# Revit family: Cleanout_Floor-Zurn-Z1400-K
name_source: partatom
category: Plumbing Fixtures
units: mm (PartAtom-declared; Revit-internal decimal feet)

## family parameters
Always vertical = Yes
Cut with Voids When Loaded = No
Maintain Annotation Orientation = No
OmniClass Number = 23.70.50.21.24.14
OmniClass Title = Deck Waste Water Drains
Part Type = Normal
Room Calculation Point = No
Round Connector Dimension = Use Radius
Shared = No
Work Plane-Based = No

## types (68) — shared parameters
Assembly Code = D2030300
CW Connection = No
Default Elevation = 20 "
Description = HEAVY-DUTY LEVEL-TROL ADJUSTABLE FLOOR CLEANOUT W/ ANCHOR FLANGE
HW Connection = No
Main Material = Iron - Zurn - Cast - Painted - Blue
Manufacturer = Zurn Water, LLC
Manufacurer Brand = Zurn
Modified Date = 02/06/2026
Product Documentation Link = https://files.zurn.com
Product Page URL = https://www.zurn.com
Product data url = https://www.bimobject.com
URL = www.zurn.com
Vent Connection = No
WFU = 1
Waste Connection = Yes
ZS = No
zero-valued in all types: CWFU, Grate Open Area, HWFU

## per-type parameters (varying)
| type | Approx. Weight (Lbs) | Connector Radius | Dimension "B" | Dimension "C" | Dimension "E" | Grate Diameter | Model | Pipe Size_A Inside Diameter | Pipe Size_A Nominal Diameter | Pipe Size_A Outer Diameter | Top Material | Type Comments | Z | ZB/ZN |
| Z1400-K 2IC | 18.1 " | 1 " | 9.5 " | 6.125 " | 6.875 " | 2.782 " | Z1400-K | 2.067 " | 2 " | 2.375 " | Iron - Zurn - Cast - Painted - Blue | Z1400-K 2 Inch Inside Caulk | Yes | No |
| Z1400-K-3IC | 18.8 " | 1.5 " | 9.5 " | 6.125 " | 6.875 " | 2.782 " | Z1400-K | 3.068 " | 3 " | 3.5 " | Iron - Zurn - Cast - Painted - Blue | Z1400-K 3 Inch Inside Caulk | Yes | No |
| Z1400-K-4IC | 20.3 " | 2 " | 11.5 " | 7.25 " | 6.875 " | 3.344 " | Z1400-K | 4.026 " | 4 " | 4.5 " | Iron - Zurn - Cast - Painted - Blue | Z1400-K 4 Inch Inside Caulk | Yes | No |
| Z1400-K-5IC | 25.2 " | 2.5 " | 11.5 " | 8.25 " | 6.875 " | 3.844 " | Z1400-K | 5.047 " | 5 " | 5.563 " | Iron - Zurn - Cast - Painted - Blue | Z1400-K 5 Inch Inside Caulk | Yes | No |
| Z1400-K-6IC | 39.2 " | 3 " | 12.25 " | 9.25 " | 6.875 " | 4.344 " | Z1400-K | 6.065 " | 6 " | 6.625 " | Iron - Zurn - Cast - Painted - Blue | Z1400-K 6 Inch Inside Caulk | Yes | No |
| Z1400-K 2NH | 11.3 " | 1 " | 7.5 " | 4.125 " | 4.625 " | 1.782 " | Z1400-K | 2.067 " | 2 " | 2.375 " | Iron - Zurn - Cast - Painted - Blue | Z1400-K 2 Inch No-Hub | Yes | No |
| Z1400-K-3NH | 10 " | 1.5 " | 7.5 " | 5.125 " | 5.375 " | 2.282 " | Z1400-K | 3.068 " | 3 " | 3.5 " | Iron - Zurn - Cast - Painted - Blue | Z1400-K 3 Inch No-Hub | Yes | No |
| Z1400-K-4NH | 12.6 " | 2 " | 7.5 " | 5.125 " | 5.375 " | 2.282 " | Z1400-K | 4.026 " | 4 " | 4.5 " | Iron - Zurn - Cast - Painted - Blue | Z1400-K 4 Inch No-Hub | Yes | No |
| Z1400-K-5NH | 20.2 " | 2.5 " | 11.5 " | 7.25 " | 7.5 " | 3.344 " | Z1400-K | 5.047 " | 5 " | 5.563 " | Iron - Zurn - Cast - Painted - Blue | Z1400-K 5 Inch No-Hub | Yes | No |
| Z1400-K-6NH | 29.2 " | 3 " | 11.5 " | 8.125 " | 4.75 " | 3.782 " | Z1400-K | 6.065 " | 6 " | 6.625 " | Iron - Zurn - Cast - Painted - Blue | Z1400-K 6 Inch No-Hub | Yes | No |
| Z1400-K-8NH | 37.9 " | 4 " | 12.25 " | 9.25 " | 7.5 " | 4.344 " | Z1400-K | 7.981 " | 8 " | 8.625 " | Iron - Zurn - Cast - Painted - Blue | Z1400-K 8 Inch No-Hub | Yes | No |
| Z1400-K 2NL | 12.2 " | 1 " | 7.5 " | 5.125 " | 5.375 " | 2.282 " | Z1400-K | 2.067 " | 2 " | 2.375 " | Iron - Zurn - Cast - Painted - Blue | Z1400-K 2 Inch Neo-Loc | Yes | No |
| Z1400-K-3NL | 12.9 " | 1.5 " | 7.5 " | 5.125 " | 5.375 " | 2.282 " | Z1400-K | 3.068 " | 3 " | 3.5 " | Iron - Zurn - Cast - Painted - Blue | Z1400-K 3 Inch Neo-Loc | Yes | No |
| Z1400-K-4NL | 14.2 " | 2 " | 7.5 " | 5.125 " | 5.375 " | 2.282 " | Z1400-K | 4.026 " | 4 " | 4.5 " | Iron - Zurn - Cast - Painted - Blue | Z1400-K 4 Inch Neo-Loc | Yes | No |
| Z1400-K-5NL | 21.3 " | 2.5 " | 11.5 " | 7.25 " | 6.5 " | 3.344 " | Z1400-K | 5.047 " | 5 " | 5.563 " | Iron - Zurn - Cast - Painted - Blue | Z1400-K 5 Inch Neo-Loc | Yes | No |
| Z1400-K-6NL | 28.9 " | 3 " | 11.5 " | 8.25 " | 5.875 " | 3.844 " | Z1400-K | 6.065 " | 6 " | 6.625 " | Iron - Zurn - Cast - Painted - Blue | Z1400-K 6 Inch Neo-Loc | Yes | No |
| Z1400-K-8NL | 31.5 " | 4 " | 12.25 " | 9.25 " | 6.5 " | 4.344 " | Z1400-K | 7.981 " | 8 " | 8.625 " | Iron - Zurn - Cast - Painted - Blue | Z1400-K 8 Inch Neo-Loc | Yes | No |
| ZB1400-K 2IC | 18.1 " | 1 " | 9.5 " | 6.125 " | 6.875 " | 2.782 " | ZB1400-K | 2.067 " | 2 " | 2.375 " | Bronze - Zurn - Polished | ZB1400-K 2 Inch Inside Caulk | No | Yes |
| ZB1400-K-3IC | 18.8 " | 1.5 " | 9.5 " | 6.125 " | 6.875 " | 2.782 " | ZB1400-K | 3.068 " | 3 " | 3.5 " | Bronze - Zurn - Polished | ZB1400-K 3 Inch Inside Caulk | No | Yes |
| ZB1400-K-4IC | 20.3 " | 2 " | 11.5 " | 7.25 " | 6.875 " | 3.344 " | ZB1400-K | 4.026 " | 4 " | 4.5 " | Bronze - Zurn - Polished | ZB1400-K 4 Inch Inside Caulk | No | Yes |
| ZB1400-K-5IC | 25.2 " | 2.5 " | 11.5 " | 8.25 " | 6.875 " | 3.844 " | ZB1400-K | 5.047 " | 5 " | 5.563 " | Bronze - Zurn - Polished | ZB1400-K 5 Inch Inside Caulk | No | Yes |
| ZB1400-K-6IC | 39.2 " | 3 " | 12.25 " | 9.25 " | 6.875 " | 4.344 " | ZB1400-K | 6.065 " | 6 " | 6.625 " | Bronze - Zurn - Polished | ZB1400-K 6 Inch Inside Caulk | No | Yes |
| ZB1400-K 2NH | 11.3 " | 1 " | 7.5 " | 4.125 " | 4.625 " | 1.782 " | ZB1400-K | 2.067 " | 2 " | 2.375 " | Bronze - Zurn - Polished | ZB1400-K 2 Inch No-Hub | No | Yes |
| ZB1400-K-3NH | 10 " | 1.5 " | 7.5 " | 5.125 " | 5.375 " | 2.282 " | ZB1400-K | 3.068 " | 3 " | 3.5 " | Bronze - Zurn - Polished | ZB1400-K 3 Inch No-Hub | No | Yes |
| ZB1400-K-4NH | 12.6 " | 2 " | 7.5 " | 5.125 " | 5.375 " | 2.282 " | ZB1400-K | 4.026 " | 4 " | 4.5 " | Bronze - Zurn - Polished | ZB1400-K 4 Inch No-Hub | No | Yes |
| ZB1400-K-5NH | 20.2 " | 2.5 " | 11.5 " | 7.25 " | 7.5 " | 3.344 " | ZB1400-K | 5.047 " | 5 " | 5.563 " | Bronze - Zurn - Polished | ZB1400-K 5 Inch No-Hub | No | Yes |
| ZB1400-K-6NH | 29.2 " | 3 " | 11.5 " | 8.125 " | 4.75 " | 3.782 " | ZB1400-K | 6.065 " | 6 " | 6.625 " | Bronze - Zurn - Polished | ZB1400-K 6 Inch No-Hub | No | Yes |
| ZB1400-K-8NH | 37.9 " | 4 " | 12.25 " | 9.25 " | 7.5 " | 4.344 " | ZB1400-K | 7.981 " | 8 " | 8.625 " | Bronze - Zurn - Polished | ZB1400-K 8 Inch No-Hub | No | Yes |
| ZB1400-K 2NL | 12.2 " | 1 " | 7.5 " | 5.125 " | 5.375 " | 2.282 " | ZB1400-K | 2.067 " | 2 " | 2.375 " | Bronze - Zurn - Polished | ZB1400-K 2 Inch Neo-Loc | No | Yes |
| ZB1400-K-3NL | 12.9 " | 1.5 " | 7.5 " | 5.125 " | 5.375 " | 2.282 " | ZB1400-K | 3.068 " | 3 " | 3.5 " | Bronze - Zurn - Polished | ZB1400-K 3 Inch Neo-Loc | No | Yes |
| ZB1400-K-4NL | 14.2 " | 2 " | 7.5 " | 5.125 " | 5.375 " | 2.282 " | ZB1400-K | 4.026 " | 4 " | 4.5 " | Bronze - Zurn - Polished | ZB1400-K 4 Inch Neo-Loc | No | Yes |
| ZB1400-K-5NL | 21.3 " | 2.5 " | 11.5 " | 7.25 " | 6.5 " | 3.344 " | ZB1400-K | 5.047 " | 5 " | 5.563 " | Bronze - Zurn - Polished | ZB1400-K 5 Inch Neo-Loc | No | Yes |
| ZB1400-K-6NL | 28.9 " | 3 " | 11.5 " | 8.25 " | 5.875 " | 3.844 " | ZB1400-K | 6.065 " | 6 " | 6.625 " | Bronze - Zurn - Polished | ZB1400-K 6 Inch Neo-Loc | No | Yes |
| ZB1400-K-8NL | 31.5 " | 4 " | 12.25 " | 9.25 " | 6.5 " | 4.344 " | ZB1400-K | 7.981 " | 8 " | 8.625 " | Bronze - Zurn - Polished | ZB1400-K 8 Inch Neo-Loc | No | Yes |
| ZN1400-K 2IC | 18.1 " | 1 " | 9.5 " | 6.125 " | 6.875 " | 2.782 " | ZN1400-K | 2.067 " | 2 " | 2.375 " | Bronze - Zurn - Polished Nickel | ZN1400-K 2 Inch Inside Caulk | No | Yes |
| ZN1400-K-3IC | 18.8 " | 1.5 " | 9.5 " | 6.125 " | 6.875 " | 2.782 " | ZN1400-K | 3.068 " | 3 " | 3.5 " | Bronze - Zurn - Polished Nickel | ZN1400-K 3 Inch Inside Caulk | No | Yes |
| ZN1400-K-4IC | 20.3 " | 2 " | 11.5 " | 7.25 " | 6.875 " | 3.344 " | ZN1400-K | 4.026 " | 4 " | 4.5 " | Bronze - Zurn - Polished Nickel | ZN1400-K 4 Inch Inside Caulk | No | Yes |
| ZN1400-K-5IC | 25.2 " | 2.5 " | 11.5 " | 8.25 " | 6.875 " | 3.844 " | ZN1400-K | 5.047 " | 5 " | 5.563 " | Bronze - Zurn - Polished Nickel | ZN1400-K 5 Inch Inside Caulk | No | Yes |
| ZN1400-K-6IC | 39.2 " | 3 " | 12.25 " | 9.25 " | 6.875 " | 4.344 " | ZN1400-K | 6.065 " | 6 " | 6.625 " | Bronze - Zurn - Polished Nickel | ZN1400-K 6 Inch Inside Caulk | No | Yes |
| ZN1400-K 2NH | 11.3 " | 1 " | 7.5 " | 4.125 " | 4.625 " | 1.782 " | ZN1400-K | 2.067 " | 2 " | 2.375 " | Bronze - Zurn - Polished Nickel | ZN1400-K 2 Inch No-Hub | No | Yes |
| ZN1400-K-3NH | 10 " | 1.5 " | 7.5 " | 5.125 " | 5.375 " | 2.282 " | ZN1400-K | 3.068 " | 3 " | 3.5 " | Bronze - Zurn - Polished Nickel | ZN1400-K 3 Inch No-Hub | No | Yes |
| ZN1400-K-4NH | 12.6 " | 2 " | 7.5 " | 5.125 " | 5.375 " | 2.282 " | ZN1400-K | 4.026 " | 4 " | 4.5 " | Bronze - Zurn - Polished Nickel | ZN1400-K 4 Inch No-Hub | No | Yes |
| ZN1400-K-5NH | 20.2 " | 2.5 " | 11.5 " | 7.25 " | 7.5 " | 3.344 " | ZN1400-K | 5.047 " | 5 " | 5.563 " | Bronze - Zurn - Polished Nickel | ZN1400-K 5 Inch No-Hub | No | Yes |
| ZN1400-K-6NH | 29.2 " | 3 " | 11.5 " | 8.125 " | 4.75 " | 3.782 " | ZN1400-K | 6.065 " | 6 " | 6.625 " | Bronze - Zurn - Polished Nickel | ZN1400-K 6 Inch No-Hub | No | Yes |
| ZN1400-K-8NH | 37.9 " | 4 " | 12.25 " | 9.25 " | 7.5 " | 4.344 " | ZN1400-K | 7.981 " | 8 " | 8.625 " | Bronze - Zurn - Polished Nickel | ZN1400-K 8 Inch No-Hub | No | Yes |
| ZN1400-K 2NL | 12.2 " | 1 " | 7.5 " | 5.125 " | 5.375 " | 2.282 " | ZN1400-K | 2.067 " | 2 " | 2.375 " | Bronze - Zurn - Polished Nickel | ZN1400-K 2 Inch Neo-Loc | No | Yes |
| ZN1400-K-3NL | 12.9 " | 1.5 " | 7.5 " | 5.125 " | 5.375 " | 2.282 " | ZN1400-K | 3.068 " | 3 " | 3.5 " | Bronze - Zurn - Polished Nickel | ZN1400-K 3 Inch Neo-Loc | No | Yes |
| ZN1400-K-4NL | 14.2 " | 2 " | 7.5 " | 5.125 " | 5.375 " | 2.282 " | ZN1400-K | 4.026 " | 4 " | 4.5 " | Bronze - Zurn - Polished Nickel | ZN1400-K 4 Inch Neo-Loc | No | Yes |
| ZN1400-K-5NL | 21.3 " | 2.5 " | 11.5 " | 7.25 " | 6.5 " | 3.344 " | ZN1400-K | 5.047 " | 5 " | 5.563 " | Bronze - Zurn - Polished Nickel | ZN1400-K 5 Inch Neo-Loc | No | Yes |
| ZN1400-K-6NL | 28.9 " | 3 " | 11.5 " | 8.25 " | 5.875 " | 3.844 " | ZN1400-K | 6.065 " | 6 " | 6.625 " | Bronze - Zurn - Polished Nickel | ZN1400-K 6 Inch Neo-Loc | No | Yes |
| ZN1400-K-8NL | 31.5 " | 4 " | 12.25 " | 9.25 " | 6.5 " | 4.344 " | ZN1400-K | 7.981 " | 8 " | 8.625 " | Bronze - Zurn - Polished Nickel | ZN1400-K 8 Inch Neo-Loc | No | Yes |
| ZS1400-K 2IC | 18.1 " | 1 " | 9.5 " | 6.125 " | 6.875 " | 2.782 " | ZS1400-K | 2.067 " | 2 " | 2.375 " | Steel - Zurn - Stainless - Type - 304 | ZS1400-K 2 Inch Inside Caulk | No | Yes |
| ZS1400-K-3IC | 18.8 " | 1.5 " | 9.5 " | 6.125 " | 6.875 " | 2.782 " | ZS1400-K | 3.068 " | 3 " | 3.5 " | Steel - Zurn - Stainless - Type - 304 | ZS1400-K 3 Inch Inside Caulk | No | Yes |
| ZS1400-K-4IC | 20.3 " | 2 " | 11.5 " | 7.25 " | 6.875 " | 3.344 " | ZS1400-K | 4.026 " | 4 " | 4.5 " | Steel - Zurn - Stainless - Type - 304 | ZS1400-K 4 Inch Inside Caulk | No | Yes |
| ZS1400-K-5IC | 25.2 " | 2.5 " | 11.5 " | 8.25 " | 6.875 " | 3.844 " | ZS1400-K | 5.047 " | 5 " | 5.563 " | Steel - Zurn - Stainless - Type - 304 | ZS1400-K 5 Inch Inside Caulk | No | Yes |
| ZS1400-K-6IC | 39.2 " | 3 " | 12.25 " | 9.25 " | 6.875 " | 4.344 " | ZS1400-K | 6.065 " | 6 " | 6.625 " | Steel - Zurn - Stainless - Type - 304 | ZS1400-K 6 Inch Inside Caulk | No | Yes |
| ZS1400-K 2NH | 11.3 " | 1 " | 7.5 " | 4.125 " | 4.625 " | 1.782 " | ZS1400-K | 2.067 " | 2 " | 2.375 " | Steel - Zurn - Stainless - Type - 304 | ZS1400-K 2 Inch No-Hub | No | Yes |
| ZS1400-K-3NH | 10 " | 1.5 " | 7.5 " | 5.125 " | 5.375 " | 2.282 " | ZS1400-K | 3.068 " | 3 " | 3.5 " | Steel - Zurn - Stainless - Type - 304 | ZS1400-K 3 Inch No-Hub | No | Yes |
| ZS1400-K-4NH | 12.6 " | 2 " | 7.5 " | 5.125 " | 5.375 " | 2.282 " | ZS1400-K | 4.026 " | 4 " | 4.5 " | Steel - Zurn - Stainless - Type - 304 | ZS1400-K 4 Inch No-Hub | No | Yes |
| ZS1400-K-5NH | 20.2 " | 2.5 " | 11.5 " | 7.25 " | 7.5 " | 3.344 " | ZS1400-K | 5.047 " | 5 " | 5.563 " | Steel - Zurn - Stainless - Type - 304 | ZS1400-K 5 Inch No-Hub | No | Yes |
| ZS1400-K-6NH | 29.2 " | 3 " | 11.5 " | 8.125 " | 4.75 " | 3.782 " | ZS1400-K | 6.065 " | 6 " | 6.625 " | Steel - Zurn - Stainless - Type - 304 | ZS1400-K 6 Inch No-Hub | No | Yes |
| ZS1400-K-8NH | 37.9 " | 4 " | 12.25 " | 9.25 " | 7.5 " | 4.344 " | ZS1400-K | 7.981 " | 8 " | 8.625 " | Steel - Zurn - Stainless - Type - 304 | ZS1400-K 8 Inch No-Hub | No | Yes |
| ZS1400-K 2NL | 12.2 " | 1 " | 7.5 " | 5.125 " | 5.375 " | 2.282 " | ZS1400-K | 2.067 " | 2 " | 2.375 " | Steel - Zurn - Stainless - Type - 304 | ZS1400-K 2 Inch Neo-Loc | No | Yes |
| ZS1400-K-3NL | 12.9 " | 1.5 " | 7.5 " | 5.125 " | 5.375 " | 2.282 " | ZS1400-K | 3.068 " | 3 " | 3.5 " | Steel - Zurn - Stainless - Type - 304 | ZS1400-K 3 Inch Neo-Loc | No | Yes |
| ZS1400-K-4NL | 14.2 " | 2 " | 7.5 " | 5.125 " | 5.375 " | 2.282 " | ZS1400-K | 4.026 " | 4 " | 4.5 " | Steel - Zurn - Stainless - Type - 304 | ZS1400-K 4 Inch Neo-Loc | No | Yes |
| ZS1400-K-5NL | 21.3 " | 2.5 " | 11.5 " | 7.25 " | 6.5 " | 3.344 " | ZS1400-K | 5.047 " | 5 " | 5.563 " | Steel - Zurn - Stainless - Type - 304 | ZS1400-K 5 Inch Neo-Loc | No | Yes |
| ZS1400-K-6NL | 28.9 " | 3 " | 11.5 " | 8.25 " | 5.875 " | 3.844 " | ZS1400-K | 6.065 " | 6 " | 6.625 " | Steel - Zurn - Stainless - Type - 304 | ZS1400-K 6 Inch Neo-Loc | No | Yes |
| ZS1400-K-8NL | 31.5 " | 4 " | 12.25 " | 9.25 " | 6.5 " | 4.344 " | ZS1400-K | 7.981 " | 8 " | 8.625 " | Steel - Zurn - Stainless - Type - 304 | ZS1400-K 8 Inch Neo-Loc | No | Yes |

## geometry (parser evidence)
native form markers: Blend x6, Sweep x2
no freeform markers — native parametric forms only
